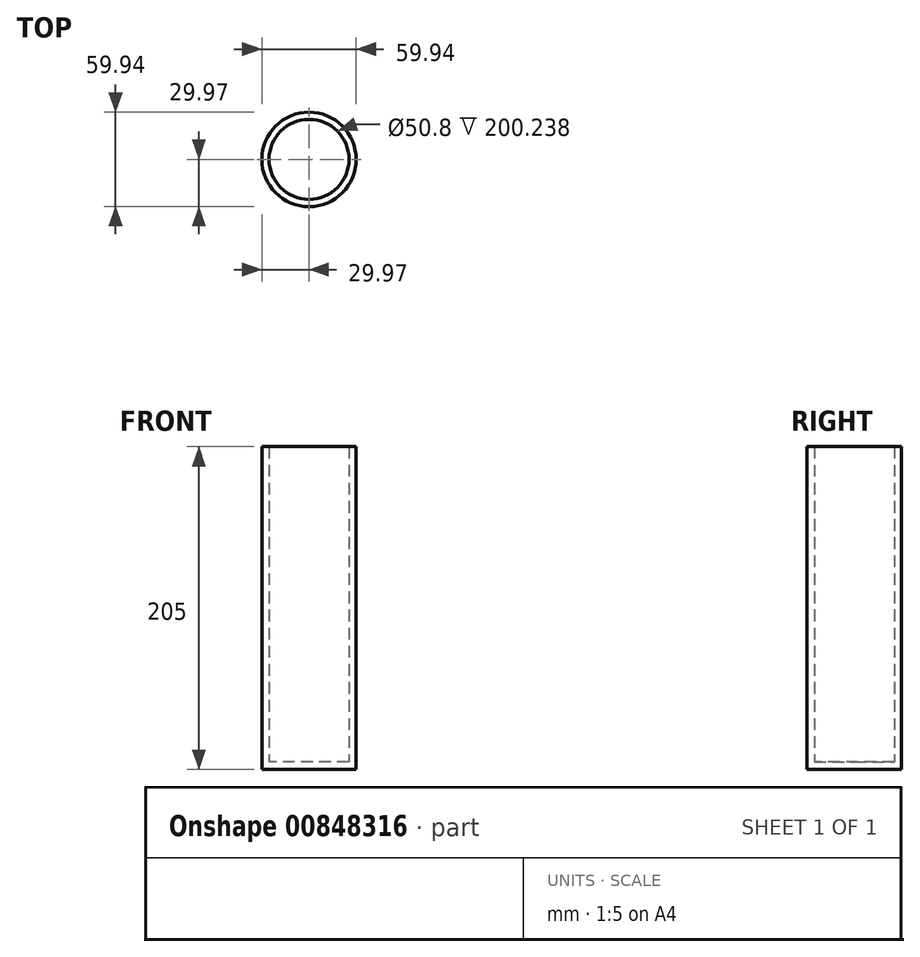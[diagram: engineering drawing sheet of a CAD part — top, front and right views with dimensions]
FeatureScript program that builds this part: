
annotation { "Feature Type Name" : "Feature", "Feature Type Description" : "" }
export const myFeature = defineFeature(function(context is Context, id is Id, definition is map)
    precondition{}
    {
        {
            var Q0;
            Q0=qCreatedBy(makeId("Top.planeOp"),FACE);
            var sketch = newSketch(context, id + "F0", { "sketchPlane" : qUnion([Q0])});
            skCircle(sketch, "E0", {"center": v(0, 0) * mm, "radius": 29.97 * mm});
            skCircle(sketch, "E1", {"center": v(0, 0) * mm, "radius": 25.4 * mm});
            skSolve(sketch);
        }
        {
            var Q0;
            Q0 = qSketchRegion(id + "F0", true);
            var Q1;
            Q1=makeQuery(id+"F0.imprint","IMPRINT",FACE,{"disambiguationData":[TD([[makeQuery(id+"F0.imprint","IMPRINT",EDGE,{"derivedFrom":sQuery(id+"F0.wireOp",EDGE,"E1")}),1.0]])]});
            extrude(context, id + "F1", {"entities" : qUnion([Q0, Q1]), "depth" : 4.76 * mm, "offsetDistance" : 25.4 * mm});
        }
        {
            var Q0;
            Q0 = qSketchRegion(id + "F0", true);
            extrude(context, id + "F2", {"entities" : qUnion([Q0]), "operationType" : NewBodyOperationType.ADD, "depth" : 205 * mm, "offsetDistance" : 25.4 * mm});
        }
    });
